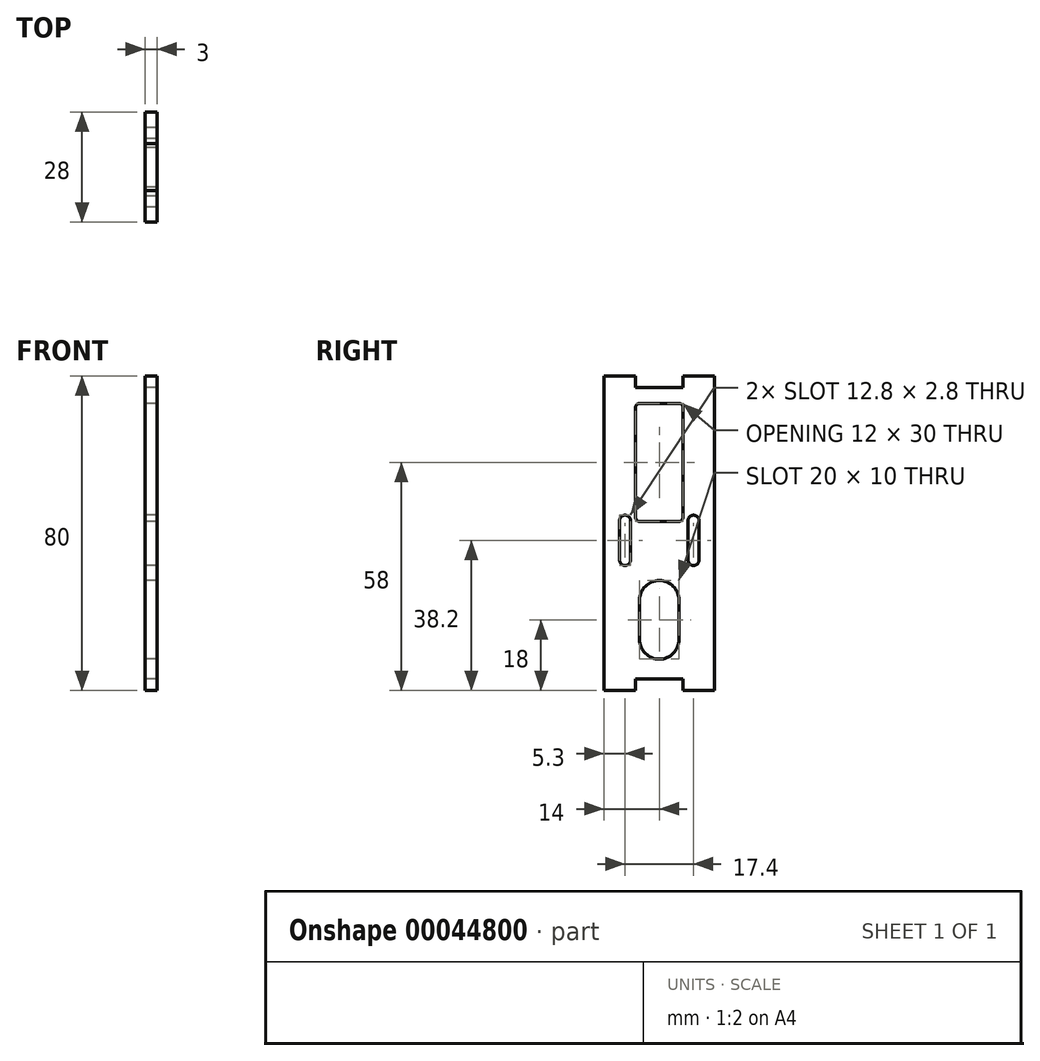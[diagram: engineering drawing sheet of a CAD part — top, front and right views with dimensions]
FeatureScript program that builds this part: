
annotation { "Feature Type Name" : "Feature", "Feature Type Description" : "" }
export const myFeature = defineFeature(function(context is Context, id is Id, definition is map)
    precondition{}
    {
        {
            var Q0;
            Q0=qCreatedBy(makeId("Right.planeOp"),FACE);
            var sketch = newSketch(context, id + "F0", { "sketchPlane" : qUnion([Q0])});
            skLineSegment(sketch, "E0.rect.bottom", {"start": v(14, 37) * mm, "end": v(-14, 37) * mm});
            skLineSegment(sketch, "E0.rect.top", {"start": v(14, -37) * mm, "end": v(-14, -37) * mm});
            skLineSegment(sketch, "E0.rect.left", {"start": v(14, 37) * mm, "end": v(14, -37) * mm});
            skLineSegment(sketch, "E0.rect.right", {"start": v(-14, 37) * mm, "end": v(-14, -37) * mm});
            skPoint(sketch, "E0.rect.middle", {"position": v(0, 0) * mm});
            skLineSegment(sketch, "E1.bottom", {"start": v(-14, 37) * mm, "end": v(-6, 37) * mm});
            skLineSegment(sketch, "E1.top", {"start": v(-14, 40) * mm, "end": v(-6, 40) * mm});
            skLineSegment(sketch, "E1.left", {"start": v(-14, 37) * mm, "end": v(-14, 40) * mm});
            skLineSegment(sketch, "E1.right", {"start": v(-6, 37) * mm, "end": v(-6, 40) * mm});
            skLineSegment(sketch, "E2.bottom", {"start": v(14, 37) * mm, "end": v(6, 37) * mm});
            skLineSegment(sketch, "E2.top", {"start": v(14, 40) * mm, "end": v(6, 40) * mm});
            skLineSegment(sketch, "E2.left", {"start": v(14, 37) * mm, "end": v(14, 40) * mm});
            skLineSegment(sketch, "E2.right", {"start": v(6, 37) * mm, "end": v(6, 40) * mm});
            skLineSegment(sketch, "E3", {"start": v(0, 37) * mm, "end": v(0, -37) * mm, "construction": true});
            skLineSegment(sketch, "E4.bottom", {"start": v(-14, -37) * mm, "end": v(-6, -37) * mm});
            skLineSegment(sketch, "E4.top", {"start": v(-14, -40) * mm, "end": v(-6, -40) * mm});
            skLineSegment(sketch, "E4.left", {"start": v(-14, -37) * mm, "end": v(-14, -40) * mm});
            skLineSegment(sketch, "E4.right", {"start": v(-6, -37) * mm, "end": v(-6, -40) * mm});
            skLineSegment(sketch, "E5.bottom", {"start": v(14, -37) * mm, "end": v(6, -37) * mm});
            skLineSegment(sketch, "E5.top", {"start": v(14, -40) * mm, "end": v(6, -40) * mm});
            skLineSegment(sketch, "E5.left", {"start": v(14, -37) * mm, "end": v(14, -40) * mm});
            skLineSegment(sketch, "E5.right", {"start": v(6, -37) * mm, "end": v(6, -40) * mm});
            skLineSegment(sketch, "E6.rect.bottom", {"start": v(5, -17) * mm, "end": v(-5, -17) * mm});
            skLineSegment(sketch, "E6.rect.top", {"start": v(5, -27) * mm, "end": v(-5, -27) * mm});
            skLineSegment(sketch, "E6.rect.left", {"start": v(5, -17) * mm, "end": v(5, -27) * mm});
            skLineSegment(sketch, "E6.rect.right", {"start": v(-5, -17) * mm, "end": v(-5, -27) * mm});
            skPoint(sketch, "E6.rect.middle", {"position": v(0, -22) * mm});
            skArc(sketch, "E7", {"start": v(5, -17) * mm, "mid": v(0, -12) * mm, "end": v(-5, -17) * mm});
            skArc(sketch, "E8", {"start": v(-5, -27) * mm, "mid": v(0, -32) * mm, "end": v(5, -27) * mm});
            skLineSegment(sketch, "E9.rect.bottom", {"start": v(-10.1, 3.2) * mm, "end": v(-7.3, 3.2) * mm});
            skLineSegment(sketch, "E9.rect.top", {"start": v(-10.1, -6.8) * mm, "end": v(-7.3, -6.8) * mm});
            skLineSegment(sketch, "E9.rect.left", {"start": v(-10.1, 3.2) * mm, "end": v(-10.1, -6.8) * mm});
            skLineSegment(sketch, "E9.rect.right", {"start": v(-7.3, 3.2) * mm, "end": v(-7.3, -6.8) * mm});
            skPoint(sketch, "E9.rect.middle", {"position": v(-8.7, -1.8) * mm});
            skArc(sketch, "E10", {"start": v(-7.3, 3.2) * mm, "mid": v(-8.7, 4.6) * mm, "end": v(-10.1, 3.2) * mm});
            skArc(sketch, "E11", {"start": v(-10.1, -6.8) * mm, "mid": v(-8.7, -8.2) * mm, "end": v(-7.3, -6.8) * mm});
            skLineSegment(sketch, "E12.rect.bottom", {"start": v(6, 33) * mm, "end": v(-6, 33) * mm});
            skLineSegment(sketch, "E12.rect.top", {"start": v(6, 3) * mm, "end": v(-6, 3) * mm});
            skLineSegment(sketch, "E12.rect.left", {"start": v(6, 33) * mm, "end": v(6, 3) * mm});
            skLineSegment(sketch, "E12.rect.right", {"start": v(-6, 33) * mm, "end": v(-6, 3) * mm});
            skPoint(sketch, "E12.rect.middle", {"position": v(0, 18) * mm});
            skLineSegment(sketch, "E13.MirrorCS", {"start": v(10.1, 3.2) * mm, "end": v(7.3, 3.2) * mm});
            skLineSegment(sketch, "E14.MirrorCS", {"start": v(10.1, -6.8) * mm, "end": v(7.3, -6.8) * mm});
            skPoint(sketch, "E15.MirrorP", {"position": v(8.7, -1.8) * mm});
            skArc(sketch, "E16.MirrorCS", {"start": v(7.3, 3.2) * mm, "mid": v(8.7, 4.6) * mm, "end": v(10.1, 3.2) * mm});
            skArc(sketch, "E17.MirrorCS", {"start": v(10.1, -6.8) * mm, "mid": v(8.7, -8.2) * mm, "end": v(7.3, -6.8) * mm});
            skLineSegment(sketch, "E18.MirrorCS", {"start": v(7.3, 3.2) * mm, "end": v(7.3, -6.8) * mm});
            skLineSegment(sketch, "E19.MirrorCS", {"start": v(10.1, 3.2) * mm, "end": v(10.1, -6.8) * mm});
            skSolve(sketch);
        }
        {
            var Q0;
            Q0=qSketchRegion(id+"F0",true);
            extrude(context, id + "F1", {"entities" : qUnion([Q0]), "depth" : 3 * mm});
        }
        {
            var Q0;
            Q0=makeQuery(id+"F1.opExtrude","SWEPT_EDGE",EDGE,{"disambiguationData":[OSD([sQuery(id+"F0.wireOp",EDGE,"E12.rect.bottom"),sQuery(id+"F0.wireOp",EDGE,"E12.rect.left")])]});
            var Q1;
            Q1=makeQuery(id+"F1.opExtrude","SWEPT_EDGE",EDGE,{"disambiguationData":[OSD([sQuery(id+"F0.wireOp",EDGE,"E12.rect.bottom"),sQuery(id+"F0.wireOp",EDGE,"E12.rect.right")])]});
            var Q2;
            Q2=makeQuery(id+"F1.opExtrude","SWEPT_EDGE",EDGE,{"disambiguationData":[OSD([sQuery(id+"F0.wireOp",EDGE,"E12.rect.top"),sQuery(id+"F0.wireOp",EDGE,"E12.rect.right")])]});
            var Q3;
            Q3=makeQuery(id+"F1.opExtrude","SWEPT_EDGE",EDGE,{"disambiguationData":[OSD([sQuery(id+"F0.wireOp",EDGE,"E12.rect.top"),sQuery(id+"F0.wireOp",EDGE,"E12.rect.left")])]});
            fillet(context, id + "F2", {"entities" : qUnion([Q0, Q1, Q2, Q3]), "radius" : 1 * mm, "tangentPropagation" : true, "allowEdgeOverflow" : false});
        }
    });
